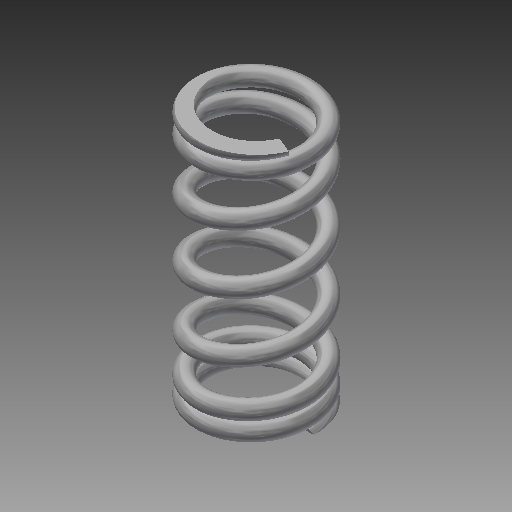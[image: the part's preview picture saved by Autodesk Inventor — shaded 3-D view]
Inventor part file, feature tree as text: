
AUTODESK INVENTOR PART (.ipt)
format: ipt  version: 2018 (Build 220112000, 112)  size: 893,952 bytes
history: native  units: mm
features: other x67, extrude x8, helix x5, sketch x3, sweep x2, plane x1
ambient origin geometry x8: Origin, YZ Plane, XZ Plane, XY Plane, X Axis, Y Axis, Z Axis, Center Point
bodies: Solid1 (feature_tree)
feature tree (86):
  other  "Main Coil Path(Right)"
  other  "Section Work Plane(Right)"
  other  "Start Work Plane(Right)"
  other  "End Work Plane(Right)"
  other  "End Cut Work Plane(Right)"
  other  "Start Cut Work Plane(Right)"
  other  "Plain Ends Cut Work Plane 1(Right)"
  other  "Plain Ends Cut Work Plane 2(Right)"
  sweep  "Main Coil Feature(R)"
  other  "Start Transition Coil 1(Right)"
  helix  "Coil  Start Transition 2(R)"  [1 undecoded]
  helix  "Coil  Start Transition 3(R)"  [1 undecoded]
  helix  "Coil  Start Transition 4(R)"  [1 undecoded]
  other  "Start Ends Coil(Right)"
  extrude  "Start Cut Feature(Right)"  Depth=10.0mm
  other  "End Transition Coil 1(Right)"
  other  "End Transition Coil 2(Right)"
  other  "End Transition Coil 3(Right)"
  other  "End Transition Coil 4(Right)"
  other  "End Coil(Right)"
  extrude  "End Cut Feature(Right)"  Depth=10.0mm
  extrude  "Plain Ends Cut Feature 1(Right)"  Depth=10.0mm
  extrude  "Plain Ends Cut  2(R)"  Depth=10.0mm TaperAngle=0.0deg
  other  "Main Coil Path(Left)"
  other  "Section Work Plane(Left)"
  other  "Start Work Plane(Left)"
  other  "End Work Plane(Left)"
  other  "End Cut Work Plane(Left)"
  other  "Start Cut Work Plane(Left)"
  other  "Plain Ends Cut Work Plane 1(Left)"
  other  "Plain Ends Cut Work Plane 2(Left)"
  sweep  "Main Coil Feature(L)"
  other  "Start Transition Coil 1(Left)"
  other  "Start Transition Coil 2(Left)"
  other  "Start Transition Coil 3(Left)"
  other  "Start Transition Coil 4(Left)"
  other  "Start Ends Coil(Left)"
  extrude  "Start Cut Feature(Left)"  Depth=10.0mm TaperAngle=0.0deg
  other  "End Transition Coil 1(Left)"
  other  "End Transition Coil 2(Left)"
  other  "End Transition Coil 3(Left)"
  other  "End Transition Coil 4(Left)"
  other  "End Coil(Left)"
  extrude  "End Cut Feature(Left)"  Depth=10.0mm
  extrude  "Cut Plain Ends Cut 1(L)"  TaperAngle=0.0deg  [1 undecoded]
  extrude  "Cut Plain Ends Cut 2(L)"  TaperAngle=0.0deg  [1 undecoded]
  other  "iMate Based Work Plane"
  other  "Preview Center Point"
  other  "Preview X Axis"
  other  "Path Section Sketch(Right)"
  other  "Srf1"
  helix  "Coil Section Sketch(Right)"  [1 undecoded]
  other  "Start Transition Coil Sketch 1(Right)"
  sketch  "Sketch  Start Transition 2(R)"  dims[d0=0.25mm d2=3.484629mm d3=10.0mm d4=26.875mm]
  sketch  "Sketch  Start Transition 3(R)"  dims[d5=0.0mm d6=90.0deg d7=90.0deg d8=0.0mm d9=0.0mm d12=2.448943mm d13=-3.186113mm d14=1.0mm]
  sketch  "Sketch  Start Transition 4(R)"  dims[d15=0.0mm d16=2.863472mm d17=10.0mm d18=2.5mm d19=0.0mm d20=90.0deg d21=90.0deg d22=0.0mm d23=0.0mm d24=2.242315mm d25=10.0mm d26=2.5mm d27=0.0mm d28=90.0deg d29=90.0deg d30=0.0mm d31=0.0mm d32=1.621157mm d33=10.0mm d34=2.5mm d35=0.0mm d36=90.0deg d37=90.0deg d38=0.0mm d39=0.0mm d40=1.0mm d41=10.0mm d42=2.5mm d43=0.0mm d44=90.0deg d45=90.0deg d46=0.0mm d47=0.0mm d48=2.863472mm d49=10.0mm d50=1.875mm d51=0.0mm d52=90.0deg d53=90.0deg d54=0.0mm d55=0.0mm d56=2.242315mm d57=10.0mm d58=1.875mm d59=0.0mm d60=90.0deg d61=90.0deg d62=0.0mm d63=0.0mm d64=1.621157mm d65=10.0mm d66=1.875mm d67=0.0mm d68=90.0deg d69=90.0deg d70=0.0mm d71=0.0mm d72=1.0mm d73=10.0mm d74=1.875mm d75=0.0mm d76=90.0deg d77=90.0deg d78=0.0mm d79=0.0mm d81=10.0mm d82=15.0mm d83=0.0mm d84=90.0deg d85=90.0deg d86=0.0mm d87=0.0mm d88=1.016944mm d89=10.0mm d90=10.0mm d91=0.0mm d92=90.0deg d93=90.0deg d94=0.0mm d95=0.0mm d96=7.0mm d97=1.016944mm d98=0.0mm d99=7.0mm d100=1.016944mm d101=0.0mm d102=0.0mm d103=0.0mm d104=0.0mm d105=0.0mm d106=0.0mm d108=0.0mm d112=0.0mm d113=0.0mm d114=0.0mm d121=0.271039mm d131=0.0mm d132=0.0mm d133=0.0mm d134=0.0mm d135=0.25mm d137=3.484629mm d138=10.0mm d139=26.875mm d140=0.0mm d141=90.0deg d142=90.0deg d143=0.0mm d144=0.0mm d145=2.448943mm d146=-3.186113mm d147=0.271039mm d148=0.016803mm d149=1.0mm d150=0.0mm d151=0.0mm d152=2.863472mm d153=10.0mm d154=2.5mm d155=0.0mm d156=90.0deg d157=90.0deg d158=0.0mm d159=0.0mm d160=2.242315mm d161=10.0mm d162=2.5mm d163=0.0mm d164=90.0deg d165=90.0deg d166=0.0mm d167=0.0mm d168=1.621157mm d169=10.0mm d170=2.5mm d171=0.0mm d172=90.0deg d173=90.0deg d174=0.0mm d175=0.0mm d176=1.0mm d177=10.0mm d178=2.5mm d179=0.0mm d180=90.0deg d181=90.0deg d182=0.0mm d183=0.0mm d184=10.0mm d185=10.0mm d186=10.0mm d187=10.0mm d188=1.016944mm d189=10.0mm d190=15.0mm d191=0.0mm d192=90.0deg d193=90.0deg d194=0.0mm d195=0.0mm d196=10.0mm d197=7.0mm d198=1.016944mm d199=0.0mm d200=10.0mm d201=2.863472mm d202=10.0mm d203=1.875mm d204=0.0mm d205=90.0deg d206=90.0deg d207=0.0mm d208=0.0mm d209=10.0mm d210=2.242315mm d211=10.0mm d212=1.875mm d213=0.0mm d214=90.0deg d215=90.0deg d216=0.0mm d217=0.0mm d218=1.621157mm d219=10.0mm d220=1.875mm d221=0.0mm d222=90.0deg d223=90.0deg d224=0.0mm d225=0.0mm d226=1.0mm d227=10.0mm d228=1.875mm d229=0.0mm d230=90.0deg d231=90.0deg d232=0.0mm d233=0.0mm d234=10.0mm d235=10.0mm d236=10.0mm d237=1.016944mm d238=10.0mm d239=10.0mm d240=0.0mm d241=90.0deg d242=90.0deg d243=0.0mm d244=0.0mm d245=7.0mm d246=1.016944mm d247=0.0mm d248=10.0mm d249=10.0mm d254=7.0mm d255=10.0mm d256=0.0mm d257=20.0mm d258=-0.016803mm d259=7.0mm d260=10.0mm d261=0.0mm d262=10.0mm d263=7.0mm d264=10.0mm d265=0.0mm d266=10.0mm d267=0.0mm d270=-3.061113mm d271=0.0mm d272=7.0mm d273=10.0mm d274=0.0mm d275=20.0mm d276=-157.079633mm d277=6.0mm d278=6.0mm d279=0.0mm d280=0.0mm]
  other  "End Transition Coil Sketch 1(Right)"
  other  "End Transition Coil Sketch 2(Right)"
  other  "End Transition Coil Sketch 3(Right)"
  other  "End Transition Coil Sketch 4(Right)"
  other  "Start Ends Skecth(Right)"
  other  "End Coil Skecth(Right)"
  other  "End Cut Sketch(Right)"
  other  "Start Cut Sketch(Right)"
  other  "Path Section Sketch(Left)"
  other  "Srf2"
  helix  "Coil Section Sketch(Left)"  [1 undecoded]
  other  "Start Transition Coil Sketch 1(Left)"
  other  "Start Transition Coil Sketch 2(Left)"
  other  "Start Transition Coil Sketch 3(Left)"
  other  "Start Transition Coil Sketch 4(Left)"
  other  "Start Ends Skecth(Left)"
  other  "Start Cut Sketch(Left)"
  other  "End Transition Coil Sketch 1(Left)"
  other  "End Transition Coil Sketch 2(Left)"
  other  "End Transition Coil Sketch 3(Left)"
  other  "End Transition Coil Sketch 4(Left)"
  other  "End Coil Skecth(Left)"
  other  "End Cut Sketch(Left)"
  other  "Plain Ends Cut Sketch 2(Left)"
  other  "Plain Ends Cut Sketch 2(Right)"
  other  "Plain Ends Cut Sketch 1(Right)"
  other  "Plain Ends Cut Sketch 1(Left)"
  plane  "Work Plane Start Section"
  other  "Basic Curve(Right)"
  other  "Basic Curve(Left)"
note: 7 required parameter values undecoded (feature->parameter linkage not recoverable at this tier; creation-order binding heuristic only, values carry confidence <= 0.55)
